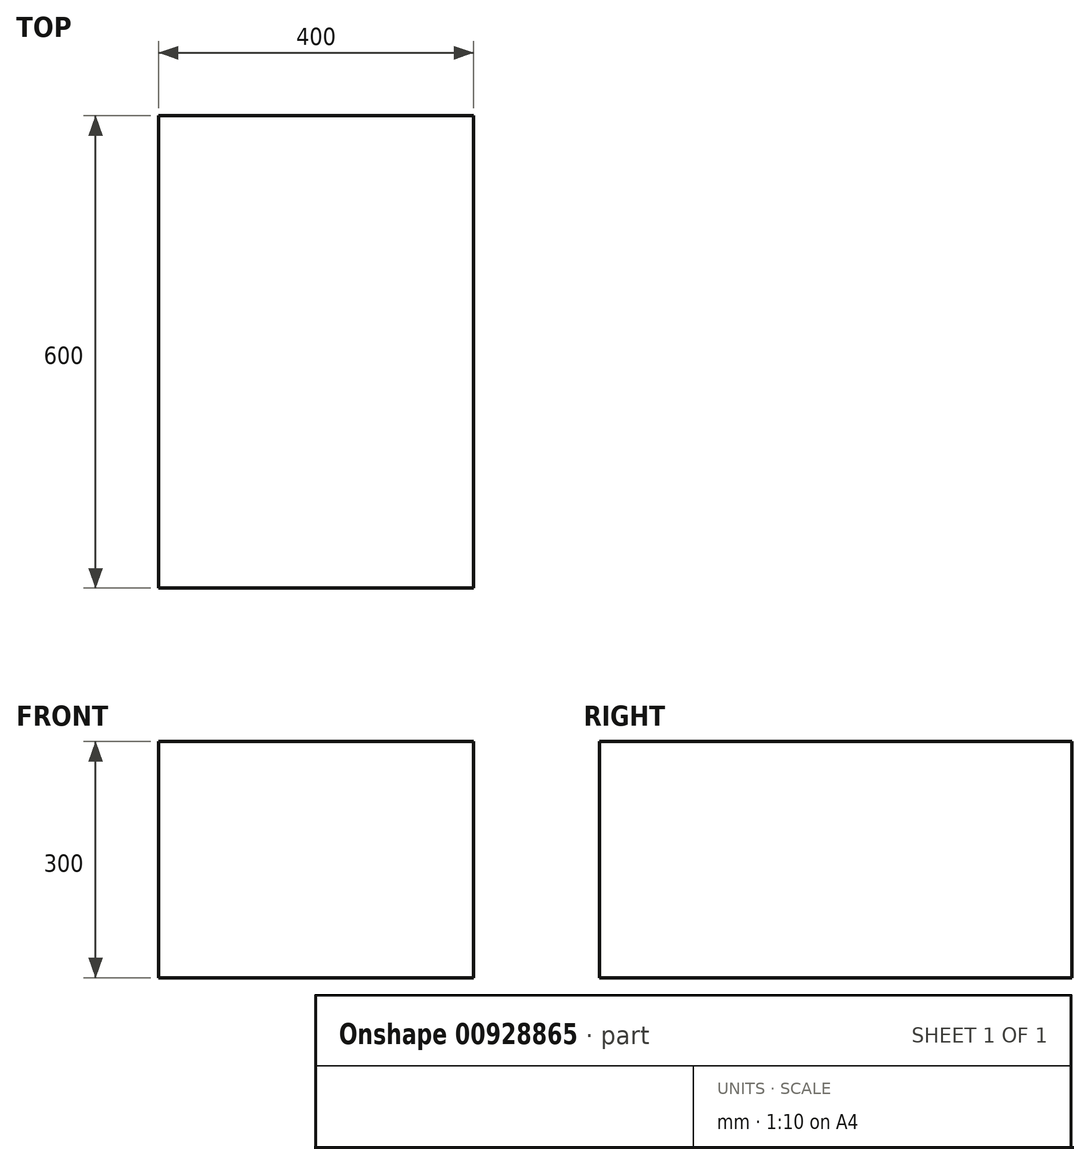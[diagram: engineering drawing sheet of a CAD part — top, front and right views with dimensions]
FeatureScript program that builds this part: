
annotation { "Feature Type Name" : "Feature", "Feature Type Description" : "" }
export const myFeature = defineFeature(function(context is Context, id is Id, definition is map)
    precondition{}
    {
        {
            var Q0;
            Q0=qCreatedBy(makeId("Top.planeOp"),FACE);
            var sketch = newSketch(context, id + "F0", { "sketchPlane" : qUnion([Q0])});
            skLineSegment(sketch, "E0.bottom", {"start": v(-197.5, -220) * mm, "end": v(202.5, -220) * mm});
            skLineSegment(sketch, "E0.top", {"start": v(-197.5, 380) * mm, "end": v(202.5, 380) * mm});
            skLineSegment(sketch, "E0.left", {"start": v(-197.5, -220) * mm, "end": v(-197.5, 380) * mm});
            skLineSegment(sketch, "E0.right", {"start": v(202.5, -220) * mm, "end": v(202.5, 380) * mm});
            skSolve(sketch);
        }
        {
            var Q0;
            Q0=makeQuery(id+"F0.imprint","IMPRINT",FACE,{"disambiguationData":[TD([[makeQuery(id+"F0.imprint","IMPRINT",EDGE,{"derivedFrom":sQuery(id+"F0.wireOp",EDGE,"E0.bottom")}),1.0]])]});
            extrude(context, id + "F1", {"entities" : qUnion([Q0]), "oppositeDirection" : true, "depth" : 300 * mm, "offsetDistance" : 25 * mm});
        }
    });
